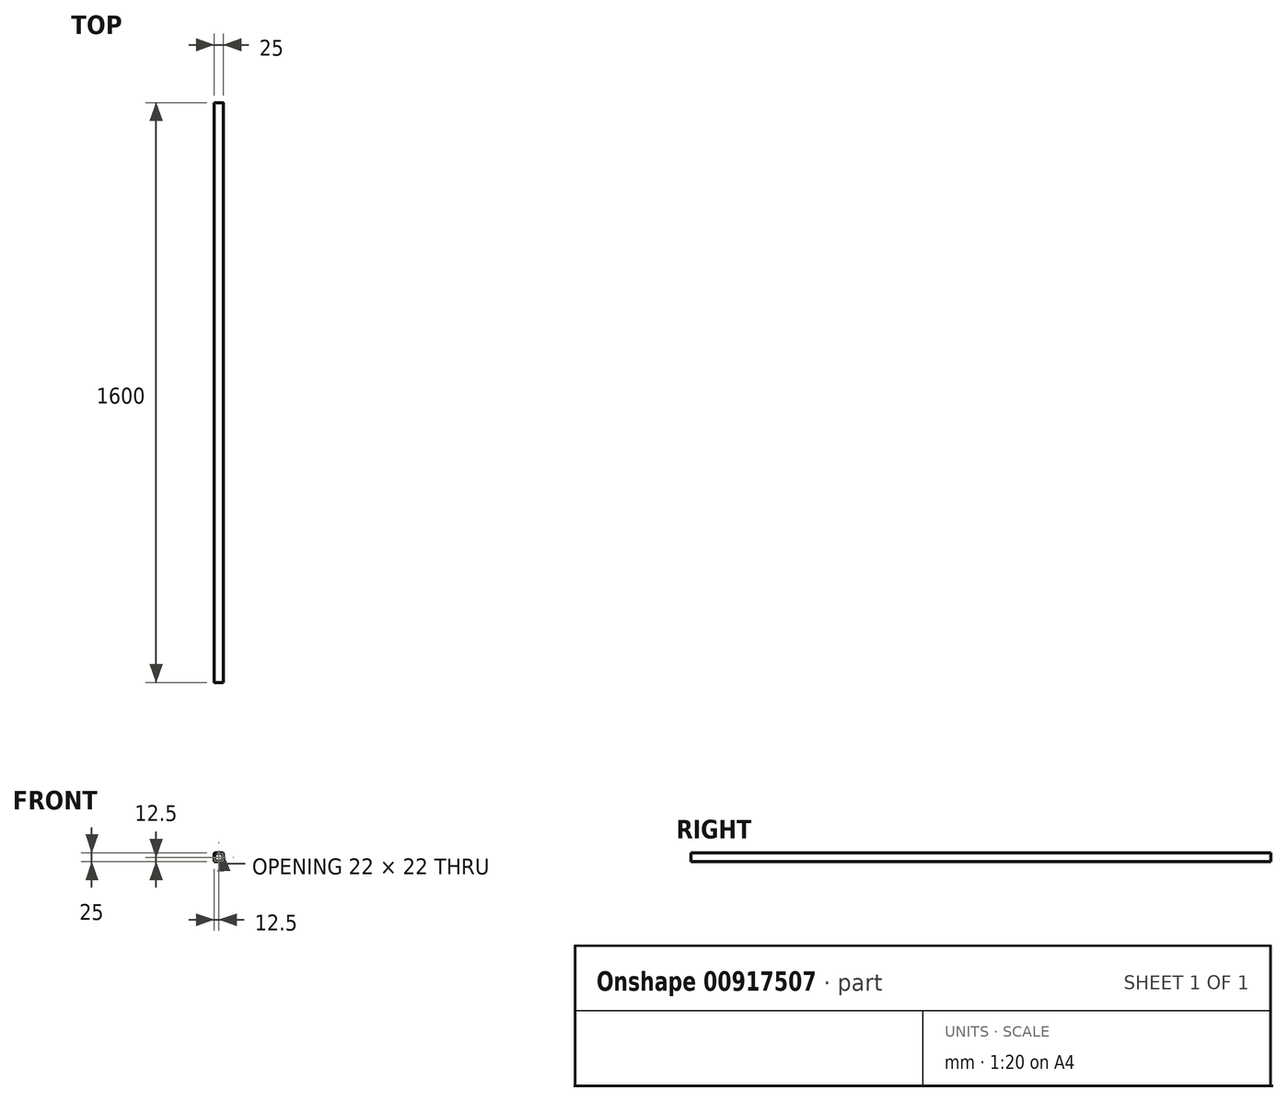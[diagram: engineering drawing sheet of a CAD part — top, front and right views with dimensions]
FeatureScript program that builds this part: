
annotation { "Feature Type Name" : "Feature", "Feature Type Description" : "" }
export const myFeature = defineFeature(function(context is Context, id is Id, definition is map)
    precondition{}
    {
        {
            var Q0;
            Q0=qCreatedBy(makeId("Front.planeOp"),FACE);
            var sketch = newSketch(context, id + "F0", { "sketchPlane" : qUnion([Q0])});
            skLineSegment(sketch, "E0.bottom", {"start": v(10, 12.5) * mm, "end": v(-10, 12.5) * mm});
            skLineSegment(sketch, "E0.top", {"start": v(10, -12.5) * mm, "end": v(-10, -12.5) * mm});
            skLineSegment(sketch, "E0.left", {"start": v(12.5, 10) * mm, "end": v(12.5, -10) * mm});
            skLineSegment(sketch, "E0.right", {"start": v(-12.5, 10) * mm, "end": v(-12.5, -10) * mm});
            skPoint(sketch, "E0.middle", {"position": v(0, 0) * mm});
            skPoint(sketch, "E1.visualSharp", {"position": v(12.5, 12.5) * mm});
            skArc(sketch, "E1.filletArc", {"start": v(12.5, 10) * mm, "mid": v(11.77, 11.77) * mm, "end": v(10, 12.5) * mm});
            skPoint(sketch, "E2.visualSharp", {"position": v(12.5, -12.5) * mm});
            skArc(sketch, "E2.filletArc", {"start": v(10, -12.5) * mm, "mid": v(11.77, -11.77) * mm, "end": v(12.5, -10) * mm});
            skPoint(sketch, "E3.visualSharp", {"position": v(-12.5, -12.5) * mm});
            skArc(sketch, "E3.filletArc", {"start": v(-12.5, -10) * mm, "mid": v(-11.77, -11.77) * mm, "end": v(-10, -12.5) * mm});
            skPoint(sketch, "E4.visualSharp", {"position": v(-12.5, 12.5) * mm});
            skArc(sketch, "E4.filletArc", {"start": v(-10, 12.5) * mm, "mid": v(-11.77, 11.77) * mm, "end": v(-12.5, 10) * mm});
            skLineSegment(sketch, "E5.0", {"start": v(11, 10) * mm, "end": v(11, -10) * mm});
            skLineSegment(sketch, "E5.1", {"start": v(10, 11) * mm, "end": v(-10, 11) * mm});
            skLineSegment(sketch, "E5.2", {"start": v(-11, 10) * mm, "end": v(-11, -10) * mm});
            skLineSegment(sketch, "E5.3", {"start": v(10, -11) * mm, "end": v(-10, -11) * mm});
            skPoint(sketch, "E6.visualSharp", {"position": v(-11, 11) * mm});
            skArc(sketch, "E6.filletArc", {"start": v(-10, 11) * mm, "mid": v(-10.7, 10.7) * mm, "end": v(-11, 10) * mm});
            skPoint(sketch, "E7.visualSharp", {"position": v(-11, -11) * mm});
            skArc(sketch, "E7.filletArc", {"start": v(-11, -10) * mm, "mid": v(-10.7, -10.7) * mm, "end": v(-10, -11) * mm});
            skPoint(sketch, "E8.visualSharp", {"position": v(11, -11) * mm});
            skArc(sketch, "E8.filletArc", {"start": v(10, -11) * mm, "mid": v(10.7, -10.7) * mm, "end": v(11, -10) * mm});
            skPoint(sketch, "E9.visualSharp", {"position": v(11, 11) * mm});
            skArc(sketch, "E9.filletArc", {"start": v(11, 10) * mm, "mid": v(10.7, 10.7) * mm, "end": v(10, 11) * mm});
            skSolve(sketch);
        }
        {
            var Q0;
            Q0=qSketchRegion(id+"F0",true);
            extrude(context, id + "F1", {"entities" : qUnion([Q0]), "depth" : 1600 * mm, "offsetDistance" : 25 * mm, "symmetric" : true});
        }
    });
